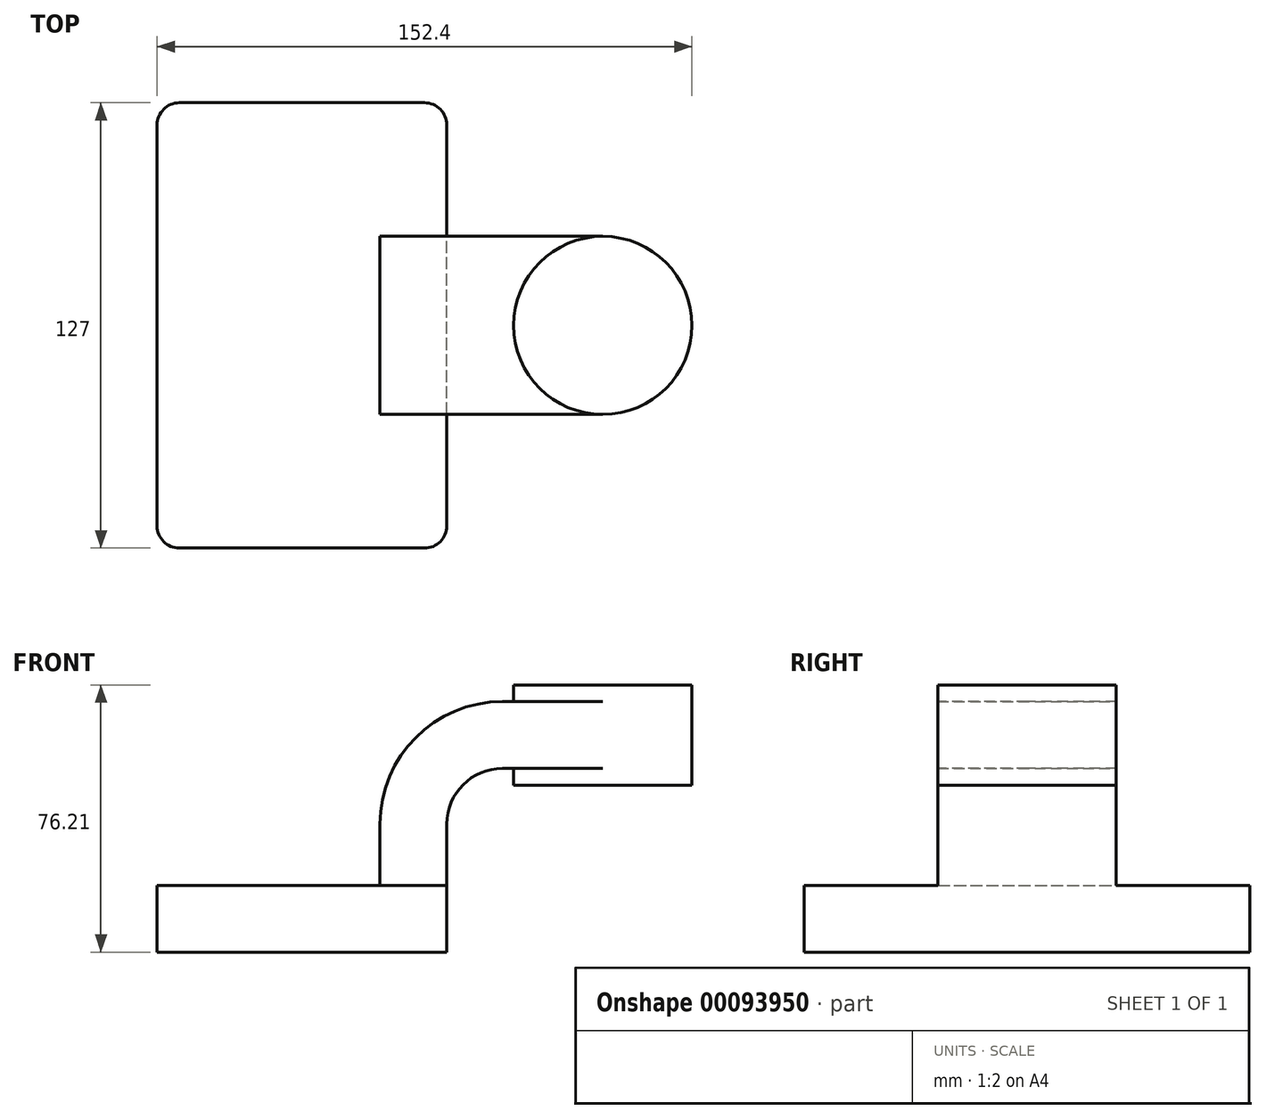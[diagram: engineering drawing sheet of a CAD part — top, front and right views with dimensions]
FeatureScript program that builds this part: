
annotation { "Feature Type Name" : "Feature", "Feature Type Description" : "" }
export const myFeature = defineFeature(function(context is Context, id is Id, definition is map)
    precondition{}
    {
        {
            var Q0;
            Q0=qCreatedBy(makeId("Front.planeOp"),FACE);
            var sketch = newSketch(context, id + "F0", { "sketchPlane" : qUnion([Q0])});
            skLineSegment(sketch, "E0.bottom", {"start": v(-41.28, -9.52) * mm, "end": v(41.28, -9.52) * mm});
            skLineSegment(sketch, "E0.top", {"start": v(-41.28, 9.53) * mm, "end": v(41.27, 9.53) * mm});
            skLineSegment(sketch, "E0.left", {"start": v(-41.27, -9.52) * mm, "end": v(-41.28, 9.53) * mm});
            skLineSegment(sketch, "E0.right", {"start": v(41.28, -9.52) * mm, "end": v(41.27, 9.53) * mm});
            skPoint(sketch, "E0.middle", {"position": v(0, 0) * mm});
            skLineSegment(sketch, "E1.bottom", {"start": v(60.32, 38.1) * mm, "end": v(111.12, 38.1) * mm});
            skLineSegment(sketch, "E1.top", {"start": v(60.32, 66.68) * mm, "end": v(111.12, 66.68) * mm});
            skLineSegment(sketch, "E1.left", {"start": v(60.32, 38.1) * mm, "end": v(60.32, 66.68) * mm});
            skLineSegment(sketch, "E1.right", {"start": v(111.13, 38.1) * mm, "end": v(111.13, 66.68) * mm});
            skPoint(sketch, "E1.middle", {"position": v(85.72, 52.39) * mm});
            skLineSegment(sketch, "E2", {"start": v(41.27, 9.53) * mm, "end": v(41.27, 26.99) * mm});
            skArc(sketch, "E3", {"start": v(41.27, 26.99) * mm, "mid": v(45.92, 38.21) * mm, "end": v(57.15, 42.86) * mm});
            skLineSegment(sketch, "E4", {"start": v(57.15, 42.86) * mm, "end": v(85.73, 42.86) * mm});
            skLineSegment(sketch, "E5.0", {"start": v(57.15, 61.91) * mm, "end": v(85.73, 61.91) * mm});
            skArc(sketch, "E5.1", {"start": v(22.22, 26.99) * mm, "mid": v(32.45, 51.68) * mm, "end": v(57.15, 61.91) * mm});
            skLineSegment(sketch, "E5.2", {"start": v(22.22, 9.53) * mm, "end": v(22.22, 26.99) * mm});
            skFitSpline(sketch, "E6", {"points": [v(-41.28, 9.53) * mm, v(57.15, 61.91) * mm], "startDerivative": vector(1.98, 93.13) * mm, "endDerivative": vector(118.97, -0.1) * mm});
            skLineSegment(sketch, "E7", {"start": v(85.72, 38.1) * mm, "end": v(85.72, 66.68) * mm});
            skSolve(sketch);
        }
        {
            var Q0;
            Q0=makeQuery(id+"F0.imprint","IMPRINT",FACE,{"disambiguationData":[TD([[makeQuery(id+"F0.imprint","IMPRINT",EDGE,{"derivedFrom":sQuery(id+"F0.wireOp",EDGE,"E0.bottom")}),1.0]])]});
            extrude(context, id + "F1", {"entities" : qUnion([Q0]), "endBound" : BoundingType.SYMMETRIC, "depth" : 127 * mm});
        }
        {
            var Q0;
            {var subQ0=sQuery(id+"F0.wireOp",EDGE,"E4");var subQ1=sQuery(id+"F0.wireOp",EDGE,"E1.left");var subQ2=makeQuery(id+"F0.imprint","INTERSECT",VERTEX,{"derivedFrom":[subQ1,subQ0]});Q0=makeQuery(id+"F0.imprint","IMPRINT",FACE,{"disambiguationData":[TD([[makeQuery(id+"F0.imprint","IMPRINT",EDGE,{"disambiguationData":[TD([[subQ2,-1.0]])],"derivedFrom":subQ1}),-1.0]])]});}
            var Q1;
            {var subQ1=sQuery(id+"F0.wireOp",EDGE,"E2");Q1=makeQuery(id+"F0.imprint","IMPRINT",FACE,{"disambiguationData":[TD([[makeQuery(id+"F0.imprint","IMPRINT",EDGE,{"derivedFrom":subQ1}),1.0]])]});}
            extrude(context, id + "F2", {"entities" : qUnion([Q0, Q1]), "operationType" : NewBodyOperationType.ADD, "endBound" : BoundingType.SYMMETRIC, "depth" : 50.8 * mm});
        }
        {
            var Q0;
            Q0=makeQuery(id+"F0.imprint","IMPRINT",FACE,{"disambiguationData":[TD([[makeQuery(id+"F0.imprint","IMPRINT",EDGE,{"derivedFrom":sQuery(id+"F0.wireOp",EDGE,"E5.1")}),1.0]])]});
            var Q1;
            Q1 = qSketchRegion(id + "FH6pZAETDrNkAko_1", true);
            extrude(context, id + "F3", {"entities" : qUnion([Q0, Q1]), "operationType" : NewBodyOperationType.ADD, "endBound" : BoundingType.SYMMETRIC, "depth" : 15.88 * mm});
        }
        {
            var Q0;
            {var subQ0=sQuery(id+"F0.wireOp",EDGE,"E1.right");Q0=makeQuery(id+"F0.imprint","IMPRINT",FACE,{"disambiguationData":[TD([[makeQuery(id+"F0.imprint","IMPRINT",EDGE,{"derivedFrom":subQ0}),1.0]])]});}
            var Q1;
            Q1=sQuery(id+"F0.wireOp",EDGE,"E7");
            revolve(context, id + "F4", {"operationType" : NewBodyOperationType.ADD, "entities" : qUnion([Q0]), "axis" : qUnion([Q1]), "revolveType" : RevolveType.FULL});
        }
        {
            var Q0;
            Q0=makeQuery(id+"F1.opExtrude","CAP_EDGE",EDGE,{"disambiguationData":[OSD([sQuery(id+"F0.wireOp",EDGE,"E0.right")])],"isStart":false});
            var Q1;
            Q1=makeQuery(id+"F1.opExtrude","CAP_EDGE",EDGE,{"disambiguationData":[OSD([sQuery(id+"F0.wireOp",EDGE,"E0.left")])],"isStart":false});
            var Q2;
            Q2=makeQuery(id+"F1.opExtrude","CAP_EDGE",EDGE,{"disambiguationData":[OSD([sQuery(id+"F0.wireOp",EDGE,"E0.right")])],"isStart":true});
            var Q3;
            Q3=makeQuery(id+"F1.opExtrude","CAP_EDGE",EDGE,{"disambiguationData":[OSD([sQuery(id+"F0.wireOp",EDGE,"E0.left")])],"isStart":true});
            fillet(context, id + "F5", {"entities" : qUnion([Q0, Q1, Q2, Q3]), "radius" : 6.35 * mm, "tangentPropagation" : true, "allowEdgeOverflow" : false});
        }
    });
